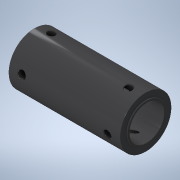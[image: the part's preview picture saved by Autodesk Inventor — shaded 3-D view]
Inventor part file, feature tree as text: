
AUTODESK INVENTOR PART (.ipt)
format: ipt  version: 2020.2 (Build 242310000, 310)  size: 901,120 bytes
history: native  units: mm
features: fillet x5, sketch x4, other x3, extrude x2, sweep x1, mirror x1, pattern_circular x1, projected_geometry x1
ambient origin geometry x8: Origin, YZ Plane, XZ Plane, XY Plane, X Axis, Y Axis, Z Axis, Center Point
bodies: Body1 (feature_tree)
feature tree (18):
  other  "Bryła1"
  extrude  "Wyciągnięcie proste1"  Depth=8.0mm
  other  "Płaszczyzna konstrukcyjna1"
  sweep  "Przeciągnięcie1"
  fillet  "Zaokrąglenie1"  Radius=26.0mm
  fillet  "Zaokrąglenie2"  Radius=1.75mm
  fillet  "Zaokrąglenie3"  Radius=3.0mm
  extrude  "Wyciągnięcie proste2"  Depth=1.0mm
  fillet  "Zaokrąglenie4"  Radius=1.25mm
  mirror  "Odbij1"
  pattern_circular  "Szyk kołowy2"  [2 undecoded]
  fillet  "Zaokrąglenie6"  Radius=1.0mm
  sketch  "Szkic1"
  sketch  "Szkic2"
  projected_geometry  "Pętla rzutowana1"
  sketch  "Szkic 3D1"
  other  "Płaszczyzna konstrukcyjna2"
  sketch  "Szkic3"
note: 2 required parameter values undecoded (feature->parameter linkage not recoverable at this tier; creation-order binding heuristic only, values carry confidence <= 0.55)
